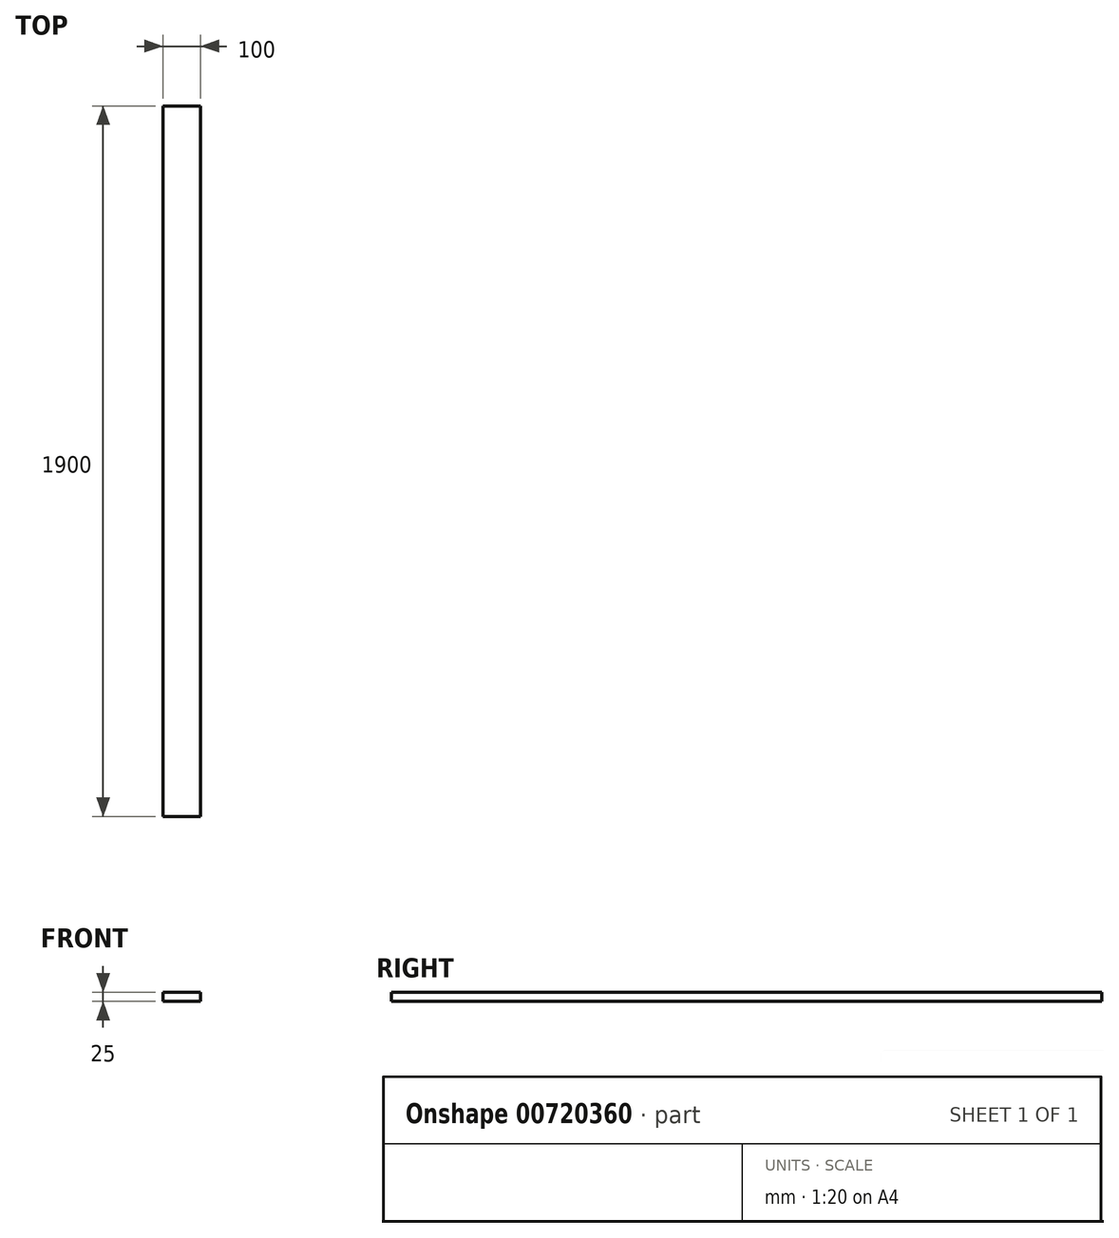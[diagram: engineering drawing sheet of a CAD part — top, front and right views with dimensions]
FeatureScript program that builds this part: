
annotation { "Feature Type Name" : "Feature", "Feature Type Description" : "" }
export const myFeature = defineFeature(function(context is Context, id is Id, definition is map)
    precondition{}
    {
        {
            var Q0;
            Q0=qCreatedBy(makeId("Right.planeOp"),FACE);
            var sketch = newSketch(context, id + "F0", { "sketchPlane" : qUnion([Q0])});
            skLineSegment(sketch, "E0.bottom", {"start": v(950, -12.5) * mm, "end": v(-950, -12.5) * mm});
            skLineSegment(sketch, "E0.top", {"start": v(950, 12.5) * mm, "end": v(-950, 12.5) * mm});
            skLineSegment(sketch, "E0.left", {"start": v(950, -12.5) * mm, "end": v(950, 12.5) * mm});
            skLineSegment(sketch, "E0.right", {"start": v(-950, -12.5) * mm, "end": v(-950, 12.5) * mm});
            skPoint(sketch, "E0.middle", {"position": v(0, 0) * mm});
            skSolve(sketch);
        }
        {
            var Q0;
            Q0=makeQuery(id+"F0.imprint","IMPRINT",FACE,{"disambiguationData":[TD([[makeQuery(id+"F0.imprint","IMPRINT",EDGE,{"derivedFrom":sQuery(id+"F0.wireOp",EDGE,"E0.bottom")}),-1.0]])]});
            extrude(context, id + "F1", {"entities" : qUnion([Q0]), "depth" : 100 * mm, "offsetDistance" : 25 * mm});
        }
    });
